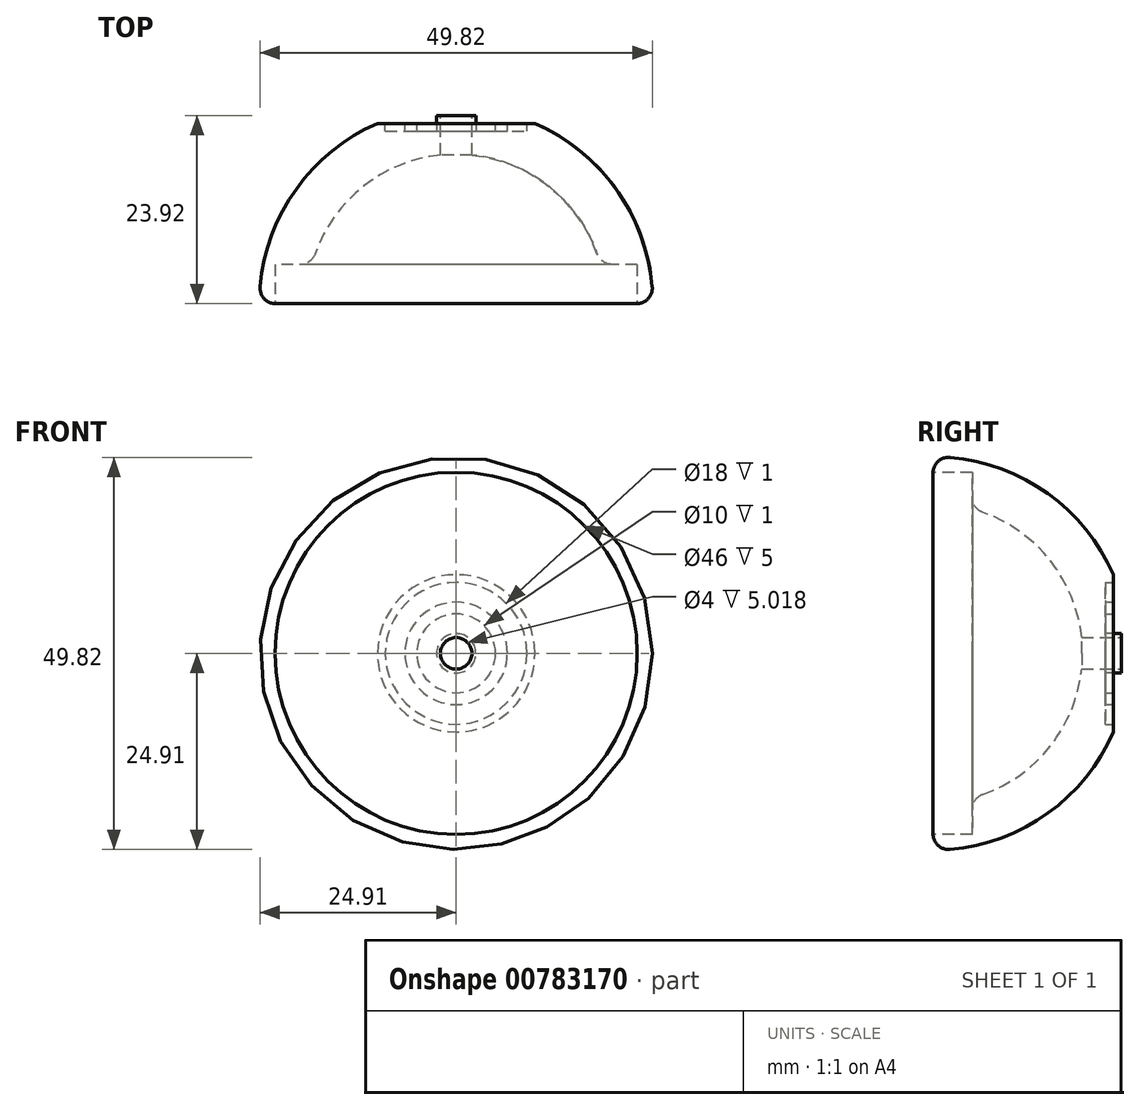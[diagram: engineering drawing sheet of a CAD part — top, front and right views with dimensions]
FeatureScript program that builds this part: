
annotation { "Feature Type Name" : "Feature", "Feature Type Description" : "" }
export const myFeature = defineFeature(function(context is Context, id is Id, definition is map)
    precondition{}
    {
        {
            var Q0;
            Q0=qCreatedBy(makeId("Top.planeOp"),FACE);
            var sketch = newSketch(context, id + "F0", { "sketchPlane" : qUnion([Q0])});
            skLineSegment(sketch, "E0", {"start": v(-45.07, -4.07) * mm, "end": v(4.93, -4.07) * mm, "construction": true});
            skArc(sketch, "E1", {"start": v(-45.07, -4.07) * mm, "mid": v(-20.07, 20.93) * mm, "end": v(4.93, -4.07) * mm});
            skLineSegment(sketch, "E2", {"start": v(-30.07, 18.85) * mm, "end": v(-10.07, 18.85) * mm});
            skLineSegment(sketch, "E3", {"start": v(-45.07, -4.07) * mm, "end": v(-39.07, -4.07) * mm});
            skLineSegment(sketch, "E4", {"start": v(4.93, -4.07) * mm, "end": v(-1.07, -4.07) * mm});
            skArc(sketch, "E5", {"start": v(-39.07, -4.07) * mm, "mid": v(-20.07, 14.93) * mm, "end": v(-1.07, -4.07) * mm});
            skLineSegment(sketch, "E6", {"start": v(-30.07, 12.09) * mm, "end": v(-10.07, 12.09) * mm});
            skLineSegment(sketch, "E7", {"start": v(-20.07, -4.07) * mm, "end": v(-20.07, 22.97) * mm});
            skPoint(sketch, "E7.endSnap0", {"position": v(-20.07, 20.93) * mm});
            skSolve(sketch);
        }
        {
            var Q0;
            {var subQ1=sQuery(id+"F0.wireOp",EDGE,"E3");Q0=makeQuery(id+"F0.imprint","IMPRINT",FACE,{"disambiguationData":[TD([[makeQuery(id+"F0.imprint","IMPRINT",EDGE,{"derivedFrom":subQ1}),1.0]])]});}
            var Q1;
            {var subQ0=sQuery(id+"F0.wireOp",EDGE,"E6");var subQ1=sQuery(id+"F0.wireOp",EDGE,"E5");var subQ2=makeQuery(id+"F0.imprint","INTERSECT",VERTEX,{"disambiguationData":[OD(0.0)],"derivedFrom":[subQ1,subQ0]});Q1=makeQuery(id+"F0.imprint","IMPRINT",FACE,{"disambiguationData":[TD([[makeQuery(id+"F0.imprint","IMPRINT",EDGE,{"disambiguationData":[TD([[subQ2,-1.0]])],"derivedFrom":subQ1}),-1.0]])]});}
            var Q2;
            Q2=sQuery(id+"F0.wireOp",EDGE,"E7");
            revolve(context, id + "F1", {"entities" : qUnion([Q0, Q1]), "axis" : qUnion([Q2]), "revolveType" : RevolveType.FULL});
        }
        {
            var Q0;
            Q0=makeQuery(id+"F1.opRevolve","SWEPT_FACE",FACE,{"disambiguationData":[OSD([sQuery(id+"F0.wireOp",EDGE,"E2")])]});
            var sketch = newSketch(context, id + "F2", { "sketchPlane" : qUnion([Q0])});
            skPoint(sketch, "E8", {"position": v(20.07, 0) * mm});
            skCircle(sketch, "E9", {"center": v(20.07, 0) * mm, "radius": 9 * mm});
            skCircle(sketch, "E10", {"center": v(20.07, 0) * mm, "radius": 6.5 * mm});
            skSolve(sketch);
        }
        {
            var Q0;
            Q0=qSketchRegion(id+"F2",true);
            extrude(context, id + "F3", {"entities" : qUnion([Q0]), "operationType" : NewBodyOperationType.REMOVE, "oppositeDirection" : true, "depth" : 1 * mm});
        }
        {
            var Q0;
            Q0=makeQuery(id+"F3.boolean.opBoolean","SPLIT",FACE,{"disambiguationData":[TD([makeQuery(id+"F3.opExtrude","SWEPT_FACE",FACE,{"disambiguationData":[OSD([sQuery(id+"F2.wireOp",EDGE,"E10")])]})])],"derivedFrom":makeQuery(id+"F1.opRevolve","SWEPT_FACE",FACE,{"disambiguationData":[OSD([sQuery(id+"F0.wireOp",EDGE,"E2")])]})});
            var sketch = newSketch(context, id + "F4", { "sketchPlane" : qUnion([Q0])});
            skPoint(sketch, "E11", {"position": v(20.07, 0) * mm});
            skCircle(sketch, "E12", {"center": v(20.07, 0) * mm, "radius": 5 * mm});
            skSolve(sketch);
        }
        {
            var Q0;
            Q0=qSketchRegion(id+"F4",true);
            extrude(context, id + "F5", {"entities" : qUnion([Q0]), "operationType" : NewBodyOperationType.REMOVE, "oppositeDirection" : true, "depth" : 1 * mm});
        }
        {
            var Q0;
            Q0=makeQuery(id+"F1.opRevolve","SWEPT_FACE",FACE,{"disambiguationData":[OSD([sQuery(id+"F0.wireOp",EDGE,"E3")])]});
            var sketch = newSketch(context, id + "F6", { "sketchPlane" : qUnion([Q0])});
            skPoint(sketch, "E13", {"position": v(-20.07, 0) * mm});
            skCircle(sketch, "E14", {"center": v(-20.07, 0) * mm, "radius": 23 * mm});
            skSolve(sketch);
        }
        {
            var Q0;
            Q0=qSketchRegion(id+"F6",true);
            extrude(context, id + "F7", {"entities" : qUnion([Q0]), "operationType" : NewBodyOperationType.REMOVE, "oppositeDirection" : true, "depth" : 5 * mm});
        }
        {
            var Q0;
            Q0=makeQuery(id+"F5.boolean.opBoolean","COPY",FACE,{"derivedFrom":makeQuery(id+"F5.opExtrude","CAP_FACE",FACE,{"disambiguationData":[OSD([sQuery(id+"F4.wireOp",EDGE,"E12")])],"isStart":false})});
            var sketch = newSketch(context, id + "F8", { "sketchPlane" : qUnion([Q0])});
            skPoint(sketch, "E15", {"position": v(20.07, 0) * mm});
            skCircle(sketch, "E16", {"center": v(20.07, 0) * mm, "radius": 2.5 * mm});
            skSolve(sketch);
        }
        {
            var Q0;
            Q0=qSketchRegion(id+"F8",true);
            extrude(context, id + "F9", {"entities" : qUnion([Q0]), "operationType" : NewBodyOperationType.ADD, "depth" : 2 * mm});
        }
        {
            var Q0;
            Q0=makeQuery(id+"F9.opExtrude","CAP_FACE",FACE,{"disambiguationData":[OSD([sQuery(id+"F8.wireOp",EDGE,"E16")])],"isStart":false});
            var sketch = newSketch(context, id + "F10", { "sketchPlane" : qUnion([Q0])});
            skPoint(sketch, "E17", {"position": v(20.07, 0) * mm});
            skCircle(sketch, "E18", {"center": v(20.07, 0) * mm, "radius": 2 * mm});
            skSolve(sketch);
        }
        {
            var Q0;
            Q0=qSketchRegion(id+"F10",true);
            extrude(context, id + "F11", {"entities" : qUnion([Q0]), "operationType" : NewBodyOperationType.REMOVE, "oppositeDirection" : true, "depth" : 25 * mm});
        }
        {
            var Q0;
            Q0=makeQuery(id+"F1.opRevolve","SWEPT_EDGE",EDGE,{"disambiguationData":[OSD([sQuery(id+"F0.wireOp",EDGE,"E1"),sQuery(id+"F0.wireOp",EDGE,"E3")])]});
            var Q1;
            Q1=makeQuery(id+"F1.opRevolve","SWEPT_EDGE",EDGE,{"disambiguationData":[OSD([sQuery(id+"F0.wireOp",EDGE,"E5"),sQuery(id+"F0.wireOp",EDGE,"E6")])]});
            var Q2;
            Q2=makeQuery(id+"F7.boolean.opBoolean","INTERSECT",EDGE,{"derivedFrom":[makeQuery(id+"F1.opRevolve","SWEPT_FACE",FACE,{"disambiguationData":[OSD([sQuery(id+"F0.wireOp",EDGE,"E5")])]}),makeQuery(id+"F7.opExtrude","CAP_FACE",FACE,{"disambiguationData":[OSD([sQuery(id+"F6.wireOp",EDGE,"E14")])],"isStart":false})]});
            fillet(context, id + "F12", {"entities" : qUnion([Q0, Q1, Q2]), "radius" : 2 * mm, "tangentPropagation" : true, "allowEdgeOverflow" : false});
        }
    });
